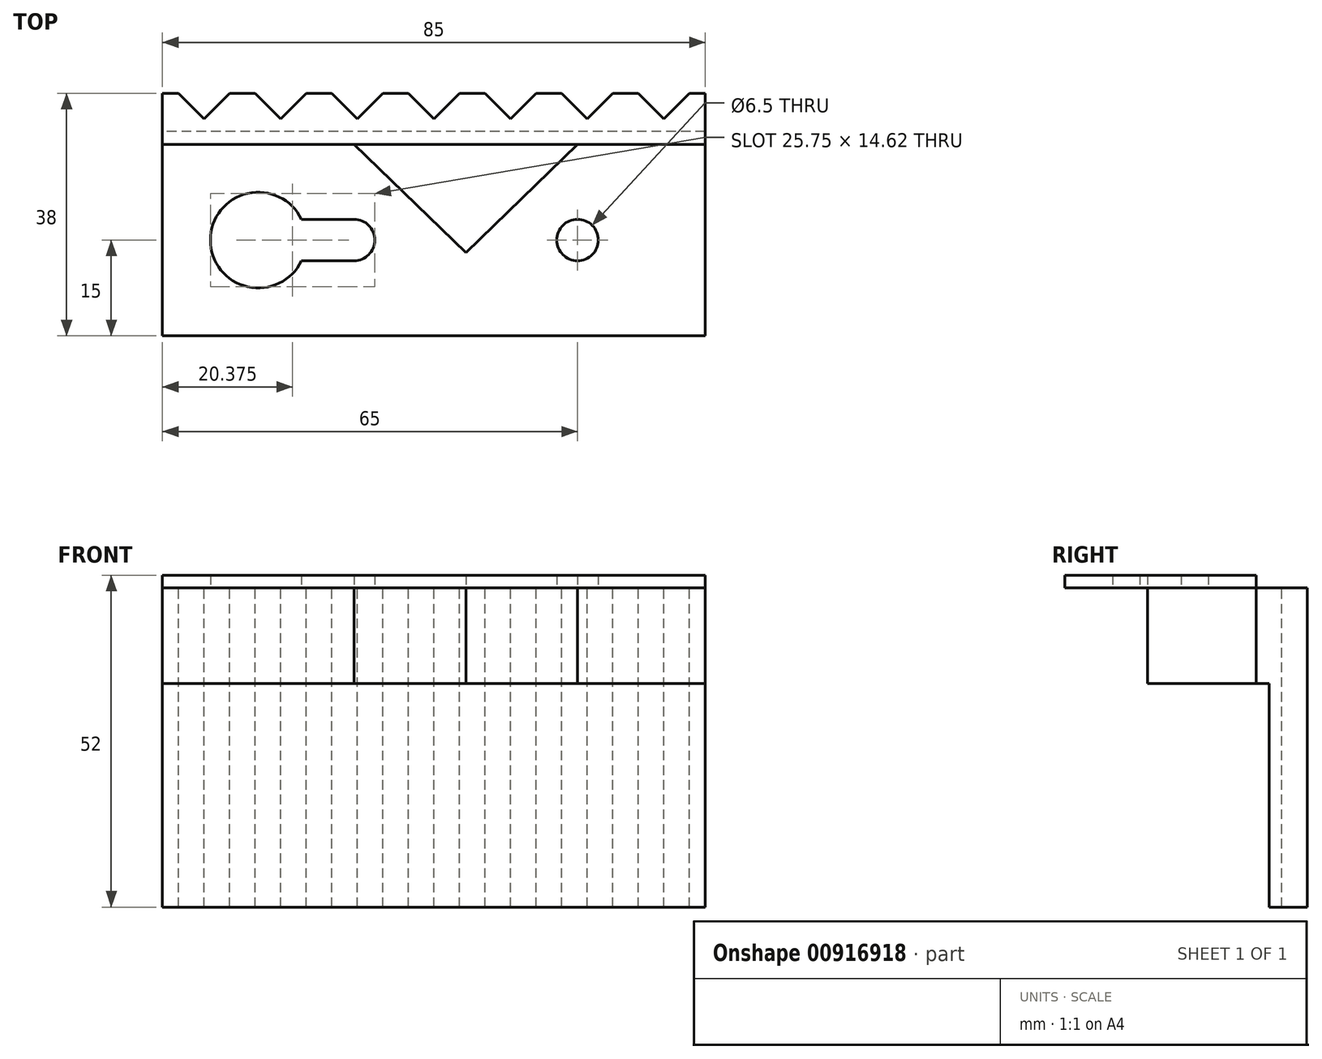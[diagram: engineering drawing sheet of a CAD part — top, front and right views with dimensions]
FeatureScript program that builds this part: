
annotation { "Feature Type Name" : "Feature", "Feature Type Description" : "" }
export const myFeature = defineFeature(function(context is Context, id is Id, definition is map)
    precondition{}
    {
        {
            var Q0;
            Q0=qCreatedBy(makeId("Top.planeOp"),FACE);
            var sketch = newSketch(context, id + "F0", { "sketchPlane" : qUnion([Q0])});
            skLineSegment(sketch, "E0.bottom", {"start": v(42.5, 15) * mm, "end": v(-42.5, 15) * mm, "construction": true});
            skLineSegment(sketch, "E0.top", {"start": v(42.5, -15) * mm, "end": v(-42.5, -15) * mm, "construction": true});
            skLineSegment(sketch, "E0.left", {"start": v(42.5, 15) * mm, "end": v(42.5, -15) * mm, "construction": true});
            skLineSegment(sketch, "E0.right", {"start": v(-42.5, 15) * mm, "end": v(-42.5, -15) * mm, "construction": true});
            skPoint(sketch, "E0.middle", {"position": v(0, 0) * mm});
            skPoint(sketch, "E1", {"position": v(-27.5, 0) * mm});
            skLineSegment(sketch, "E2", {"start": v(-42.5, 0) * mm, "end": v(-27.5, 0) * mm, "construction": true});
            skCircle(sketch, "E3", {"center": v(-27.5, 0) * mm, "radius": 7.5 * mm, "construction": true});
            skLineSegment(sketch, "E4.bottom", {"start": v(40, 17.5) * mm, "end": v(-40, 17.5) * mm, "construction": true});
            skLineSegment(sketch, "E4.top", {"start": v(40, -17.5) * mm, "end": v(-40, -17.5) * mm, "construction": true});
            skLineSegment(sketch, "E4.left", {"start": v(40, 17.5) * mm, "end": v(40, -17.5) * mm, "construction": true});
            skLineSegment(sketch, "E4.right", {"start": v(-40, 17.5) * mm, "end": v(-40, -17.5) * mm, "construction": true});
            skLineSegment(sketch, "E5", {"start": v(-42.5, 15) * mm, "end": v(-42.5, -15) * mm});
            skLineSegment(sketch, "E6", {"start": v(42.5, -15) * mm, "end": v(42.5, 15) * mm});
            skLineSegment(sketch, "E7", {"start": v(-42.5, -15) * mm, "end": v(42.5, -15) * mm});
            skPoint(sketch, "E8", {"position": v(-12.5, 0) * mm});
            skCircle(sketch, "E9", {"center": v(-12.5, 0) * mm, "radius": 3.25 * mm, "construction": true});
            skPoint(sketch, "E10", {"position": v(22.5, 0) * mm});
            skCircle(sketch, "E11", {"center": v(22.5, 0) * mm, "radius": 3.25 * mm, "construction": true});
            skLineSegment(sketch, "E12", {"start": v(-12.5, 0) * mm, "end": v(-12.5, 3.25) * mm, "construction": true});
            skLineSegment(sketch, "E13", {"start": v(-12.5, 3.25) * mm, "end": v(-20.74, 3.25) * mm, "construction": true});
            skLineSegment(sketch, "E14", {"start": v(-12.5, 0) * mm, "end": v(-12.5, -3.25) * mm, "construction": true});
            skLineSegment(sketch, "E15", {"start": v(-12.5, -3.25) * mm, "end": v(-20.74, -3.25) * mm, "construction": true});
            skLineSegment(sketch, "E16", {"start": v(-20.74, 3.25) * mm, "end": v(-12.5, 3.25) * mm});
            skLineSegment(sketch, "E17", {"start": v(-20.74, -3.25) * mm, "end": v(-12.5, -3.25) * mm});
            skPoint(sketch, "E18", {"position": v(-35, 0) * mm});
            skArc(sketch, "E19", {"start": v(-20.74, -3.25) * mm, "mid": v(-35, 0) * mm, "end": v(-20.74, 3.25) * mm});
            skArc(sketch, "E20", {"start": v(-12.5, 3.25) * mm, "mid": v(-9.25, 0) * mm, "end": v(-12.5, -3.25) * mm});
            skCircle(sketch, "E21", {"center": v(22.5, 0) * mm, "radius": 3.25 * mm});
            skPoint(sketch, "E22", {"position": v(5, 15) * mm});
            skPoint(sketch, "E23", {"position": v(-12.5, 15) * mm});
            skPoint(sketch, "E24", {"position": v(22.5, 15) * mm});
            skLineSegment(sketch, "E25", {"start": v(5, 15) * mm, "end": v(5, -15) * mm, "construction": true});
            skPoint(sketch, "E26", {"position": v(5, -2) * mm});
            skLineSegment(sketch, "E27", {"start": v(-42.5, 15) * mm, "end": v(-12.5, 15) * mm});
            skLineSegment(sketch, "E28", {"start": v(22.5, 15) * mm, "end": v(42.5, 15) * mm});
            skLineSegment(sketch, "E29", {"start": v(-12.5, 15) * mm, "end": v(5, -2) * mm});
            skLineSegment(sketch, "E30", {"start": v(22.5, 15) * mm, "end": v(5, -2) * mm});
            skLineSegment(sketch, "E31", {"start": v(22.5, 15) * mm, "end": v(-12.5, 15) * mm});
            skSolve(sketch);
        }
        {
            var Q0;
            Q0=makeQuery(id+"F0.imprint","IMPRINT",FACE,{"disambiguationData":[TD([[makeQuery(id+"F0.imprint","IMPRINT",EDGE,{"derivedFrom":sQuery(id+"F0.wireOp",EDGE,"E5")}),1.0]])]});
            extrude(context, id + "F1", {"entities" : qUnion([Q0]), "depth" : 2 * mm, "offsetDistance" : 25 * mm});
        }
        {
            var Q0;
            Q0=makeQuery(id+"F1.opExtrude","SWEPT_FACE",FACE,{"disambiguationData":[OSD([sQuery(id+"F0.wireOp",EDGE,"E28")])]});
            var sketch = newSketch(context, id + "F2", { "sketchPlane" : qUnion([Q0])});
            skLineSegment(sketch, "E32", {"start": v(-42.5, 0) * mm, "end": v(42.5, 0) * mm, "construction": true});
            skPoint(sketch, "E33", {"position": v(42.5, 0) * mm});
            skLineSegment(sketch, "E34", {"start": v(42.5, 0) * mm, "end": v(42.5, -15) * mm});
            skLineSegment(sketch, "E35", {"start": v(-42.5, 0) * mm, "end": v(-42.5, -15) * mm});
            skLineSegment(sketch, "E36", {"start": v(-42.5, -15) * mm, "end": v(42.5, -15) * mm});
            skLineSegment(sketch, "E37", {"start": v(-42.5, 0) * mm, "end": v(42.5, 0) * mm});
            skLineSegment(sketch, "E38", {"start": v(42.5, 2.02) * mm, "end": v(-42.5, 2) * mm});
            skSolve(sketch);
        }
        {
            var Q0;
            Q0=makeQuery(id+"F0.imprint","IMPRINT",FACE,{"disambiguationData":[TD([[makeQuery(id+"F0.imprint","IMPRINT",EDGE,{"derivedFrom":sQuery(id+"F0.wireOp",EDGE,"E29")}),1.0]])]});
            extrude(context, id + "F3", {"entities" : qUnion([Q0]), "operationType" : NewBodyOperationType.ADD, "oppositeDirection" : true, "depth" : 15 * mm, "offsetDistance" : 25 * mm});
        }
        {
            var Q0;
            {var subQ3=sQuery(id+"F2.wireOp",EDGE,"E34");Q0=makeQuery(id+"F2.imprint","IMPRINT",FACE,{"disambiguationData":[TD([[makeQuery(id+"F2.imprint","IMPRINT",EDGE,{"derivedFrom":subQ3}),-1.0]])]});}
            extrude(context, id + "F4", {"entities" : qUnion([Q0]), "operationType" : NewBodyOperationType.ADD, "depth" : 2 * mm, "offsetDistance" : 25 * mm});
        }
        {
            var Q0;
            Q0=makeQuery(id+"F0.imprint","IMPRINT",FACE,{"disambiguationData":[TD([[makeQuery(id+"F0.imprint","IMPRINT",EDGE,{"derivedFrom":sQuery(id+"F0.wireOp",EDGE,"E29")}),1.0]])]});
            extrude(context, id + "F5", {"entities" : qUnion([Q0]), "depth" : 2 * mm, "offsetDistance" : 25 * mm});
        }
        {
            var Q0;
            Q0=makeQuery(id+"F4.opExtrude","CAP_FACE",FACE,{"disambiguationData":[OSD([sQuery(id+"F2.wireOp",EDGE,"E34"),sQuery(id+"F2.wireOp",EDGE,"E35"),sQuery(id+"F2.wireOp",EDGE,"E36"),sQuery(id+"F2.wireOp",EDGE,"E37")])],"isStart":false});
            var sketch = newSketch(context, id + "F6", { "sketchPlane" : qUnion([Q0])});
            skSolve(sketch);
        }
        {
            var Q0;
            Q0=makeQuery(id+"F6.imprint","IMPRINT",FACE,{"disambiguationData":[TD([[makeQuery(id+"F6.imprint","IMPRINT",EDGE,{"derivedFrom":makeQuery(id+"F4.opExtrude","CAP_EDGE",EDGE,{"disambiguationData":[OSD([sQuery(id+"F2.wireOp",EDGE,"E34")])],"isStart":false})}),-1.0]])]});
            var sketch = newSketch(context, id + "F7", { "sketchPlane" : qUnion([Q0])});
            skLineSegment(sketch, "E39", {"start": v(0, 0) * mm, "end": v(-42.5, 0) * mm});
            skLineSegment(sketch, "E40", {"start": v(0, 0) * mm, "end": v(42.5, 0) * mm});
            skLineSegment(sketch, "E41", {"start": v(-42.5, 0) * mm, "end": v(-42.5, -50) * mm});
            skLineSegment(sketch, "E42", {"start": v(42.5, 0) * mm, "end": v(42.5, -50) * mm});
            skLineSegment(sketch, "E43", {"start": v(-42.5, -50) * mm, "end": v(42.5, -50) * mm});
            skSolve(sketch);
        }
        {
            var Q0;
            {var subQ2=sQuery(id+"F7.wireOp",EDGE,"E43");Q0=makeQuery(id+"F7.imprint","IMPRINT",FACE,{"disambiguationData":[TD([[makeQuery(id+"F7.imprint","IMPRINT",EDGE,{"derivedFrom":subQ2}),1.0]])]});}
            var Q1;
            Q1=makeQuery(id+"F6.imprint","IMPRINT",FACE,{"disambiguationData":[TD([[makeQuery(id+"F6.imprint","IMPRINT",EDGE,{"derivedFrom":makeQuery(id+"F4.opExtrude","CAP_EDGE",EDGE,{"disambiguationData":[OSD([sQuery(id+"F2.wireOp",EDGE,"E34")])],"isStart":false})}),-1.0]])]});
            extrude(context, id + "F8", {"entities" : qUnion([Q0, Q1]), "operationType" : NewBodyOperationType.ADD, "depth" : 2 * mm, "offsetDistance" : 25 * mm});
        }
        {
            var Q0;
            {var subQ0=sQuery(id+"F2.wireOp",EDGE,"E37");Q0=makeQuery(id+"F8.boolean.opBoolean","MERGE",FACE,{"derivedFrom":[makeQuery(id+"F4.boolean.opBoolean","MERGE",FACE,{"derivedFrom":[makeQuery(id+"F3.opExtrude","CAP_FACE",FACE,{"disambiguationData":[OSD([sQuery(id+"F0.wireOp",EDGE,"E29"),sQuery(id+"F0.wireOp",EDGE,"E30"),sQuery(id+"F0.wireOp",EDGE,"E31")])],"isStart":true}),makeQuery(id+"F4.opExtrude","SWEPT_FACE",FACE,{"disambiguationData":[OSD([subQ0])]})]}),makeQuery(id+"F8.opExtrude","SWEPT_FACE",FACE,{"disambiguationData":[OSD([subQ0])]})]});}
            var sketch = newSketch(context, id + "F9", { "sketchPlane" : qUnion([Q0])});
            skLineSegment(sketch, "E44.bottom", {"start": v(-42.5, 19) * mm, "end": v(42.5, 19) * mm, "construction": true});
            skLineSegment(sketch, "E44.top", {"start": v(-42.5, 23) * mm, "end": v(42.5, 23) * mm, "construction": true});
            skLineSegment(sketch, "E44.left", {"start": v(-42.5, 19) * mm, "end": v(-42.5, 23) * mm, "construction": true});
            skLineSegment(sketch, "E44.right", {"start": v(42.5, 19) * mm, "end": v(42.5, 23) * mm, "construction": true});
            skPoint(sketch, "E45", {"position": v(0, 19) * mm});
            skLineSegment(sketch, "E46", {"start": v(0, 19) * mm, "end": v(4, 23) * mm});
            skLineSegment(sketch, "E47", {"start": v(0, 19) * mm, "end": v(-4, 23) * mm});
            skLineSegment(sketch, "E48.1.0.0", {"start": v(12, 19) * mm, "end": v(8, 23) * mm});
            skLineSegment(sketch, "E48.1.0.1", {"start": v(12, 19) * mm, "end": v(16, 23) * mm});
            skLineSegment(sketch, "E48.2.0.0", {"start": v(24, 19) * mm, "end": v(20, 23) * mm});
            skLineSegment(sketch, "E48.2.0.1", {"start": v(24, 19) * mm, "end": v(28, 23) * mm});
            skLineSegment(sketch, "E48.3.0.0", {"start": v(36, 19) * mm, "end": v(32, 23) * mm});
            skLineSegment(sketch, "E48.3.0.1", {"start": v(36, 19) * mm, "end": v(40, 23) * mm});
            skLineSegment(sketch, "E48.direction1", {"start": v(0, 19) * mm, "end": v(12, 19) * mm, "construction": true});
            skLineSegment(sketch, "E49", {"start": v(4, 23) * mm, "end": v(8, 23) * mm});
            skLineSegment(sketch, "E50", {"start": v(16, 23) * mm, "end": v(20, 23) * mm});
            skLineSegment(sketch, "E51", {"start": v(28, 23) * mm, "end": v(32, 23) * mm});
            skLineSegment(sketch, "E52", {"start": v(40, 23) * mm, "end": v(42.5, 23) * mm});
            skLineSegment(sketch, "E53", {"start": v(42.5, 19) * mm, "end": v(42.5, 23) * mm});
            skLineSegment(sketch, "E54.1.0.0", {"start": v(-12, 19) * mm, "end": v(-16, 23) * mm});
            skLineSegment(sketch, "E54.1.0.1", {"start": v(-12, 19) * mm, "end": v(-8, 23) * mm});
            skLineSegment(sketch, "E54.2.0.0", {"start": v(-24, 19) * mm, "end": v(-28, 23) * mm});
            skLineSegment(sketch, "E54.2.0.1", {"start": v(-24, 19) * mm, "end": v(-20, 23) * mm});
            skLineSegment(sketch, "E54.3.0.0", {"start": v(-36, 19) * mm, "end": v(-40, 23) * mm});
            skLineSegment(sketch, "E54.3.0.1", {"start": v(-36, 19) * mm, "end": v(-32, 23) * mm});
            skLineSegment(sketch, "E54.direction1", {"start": v(0, 19) * mm, "end": v(-12, 19) * mm, "construction": true});
            skLineSegment(sketch, "E55", {"start": v(-40, 23) * mm, "end": v(-42.5, 23) * mm});
            skLineSegment(sketch, "E56", {"start": v(-42.5, 23) * mm, "end": v(-42.5, 19) * mm});
            skLineSegment(sketch, "E57", {"start": v(-32, 23) * mm, "end": v(-28, 23) * mm});
            skLineSegment(sketch, "E58", {"start": v(-20, 23) * mm, "end": v(-16, 23) * mm});
            skLineSegment(sketch, "E59", {"start": v(-8, 23) * mm, "end": v(-4, 23) * mm});
            skSolve(sketch);
        }
        {
            var Q0;
            {var subQ0=sQuery(id+"F9.wireOp",EDGE,"E54.3.0.0");Q0=makeQuery(id+"F9.imprint","IMPRINT",FACE,{"disambiguationData":[TD([[makeQuery(id+"F9.imprint","IMPRINT",EDGE,{"derivedFrom":subQ0}),1.0]])]});}
            var Q1;
            {var subQ0=sQuery(id+"F9.wireOp",EDGE,"E54.2.0.0");Q1=makeQuery(id+"F9.imprint","IMPRINT",FACE,{"disambiguationData":[TD([[makeQuery(id+"F9.imprint","IMPRINT",EDGE,{"derivedFrom":subQ0}),1.0]])]});}
            var Q2;
            {var subQ0=sQuery(id+"F9.wireOp",EDGE,"E54.1.0.0");Q2=makeQuery(id+"F9.imprint","IMPRINT",FACE,{"disambiguationData":[TD([[makeQuery(id+"F9.imprint","IMPRINT",EDGE,{"derivedFrom":subQ0}),1.0]])]});}
            var Q3;
            {var subQ0=sQuery(id+"F9.wireOp",EDGE,"E47");Q3=makeQuery(id+"F9.imprint","IMPRINT",FACE,{"disambiguationData":[TD([[makeQuery(id+"F9.imprint","IMPRINT",EDGE,{"derivedFrom":subQ0}),1.0]])]});}
            var Q4;
            {var subQ0=sQuery(id+"F9.wireOp",EDGE,"E46");Q4=makeQuery(id+"F9.imprint","IMPRINT",FACE,{"disambiguationData":[TD([[makeQuery(id+"F9.imprint","IMPRINT",EDGE,{"derivedFrom":subQ0}),-1.0]])]});}
            var Q5;
            {var subQ0=sQuery(id+"F9.wireOp",EDGE,"E48.1.0.1");Q5=makeQuery(id+"F9.imprint","IMPRINT",FACE,{"disambiguationData":[TD([[makeQuery(id+"F9.imprint","IMPRINT",EDGE,{"derivedFrom":subQ0}),-1.0]])]});}
            var Q6;
            {var subQ0=sQuery(id+"F9.wireOp",EDGE,"E48.2.0.1");Q6=makeQuery(id+"F9.imprint","IMPRINT",FACE,{"disambiguationData":[TD([[makeQuery(id+"F9.imprint","IMPRINT",EDGE,{"derivedFrom":subQ0}),-1.0]])]});}
            var Q7;
            {var subQ0=sQuery(id+"F9.wireOp",EDGE,"E48.3.0.1");Q7=makeQuery(id+"F9.imprint","IMPRINT",FACE,{"disambiguationData":[TD([[makeQuery(id+"F9.imprint","IMPRINT",EDGE,{"derivedFrom":subQ0}),-1.0]])]});}
            extrude(context, id + "F10", {"entities" : qUnion([Q0, Q1, Q2, Q3, Q4, Q5, Q6, Q7]), "operationType" : NewBodyOperationType.ADD, "oppositeDirection" : true, "depth" : 50 * mm, "offsetDistance" : 25 * mm});
        }
        {
            var Q0;
            Q0=makeQuery(id+"F5.opExtrude","SWEPT_BODY",BODY,{"disambiguationData":[OSD([sQuery(id+"F0.wireOp",EDGE,"E29"),sQuery(id+"F0.wireOp",EDGE,"E30"),sQuery(id+"F0.wireOp",EDGE,"E31")])]});
            transform(context, id + "F11", {"entities" : qUnion([Q0]), "transformType" : TransformType.TRANSLATION_3D, "dx" : 0 * mm, "dy" : 0 * mm, "dz" : 0 * mm, "makeCopy" : true});
        }
    });
